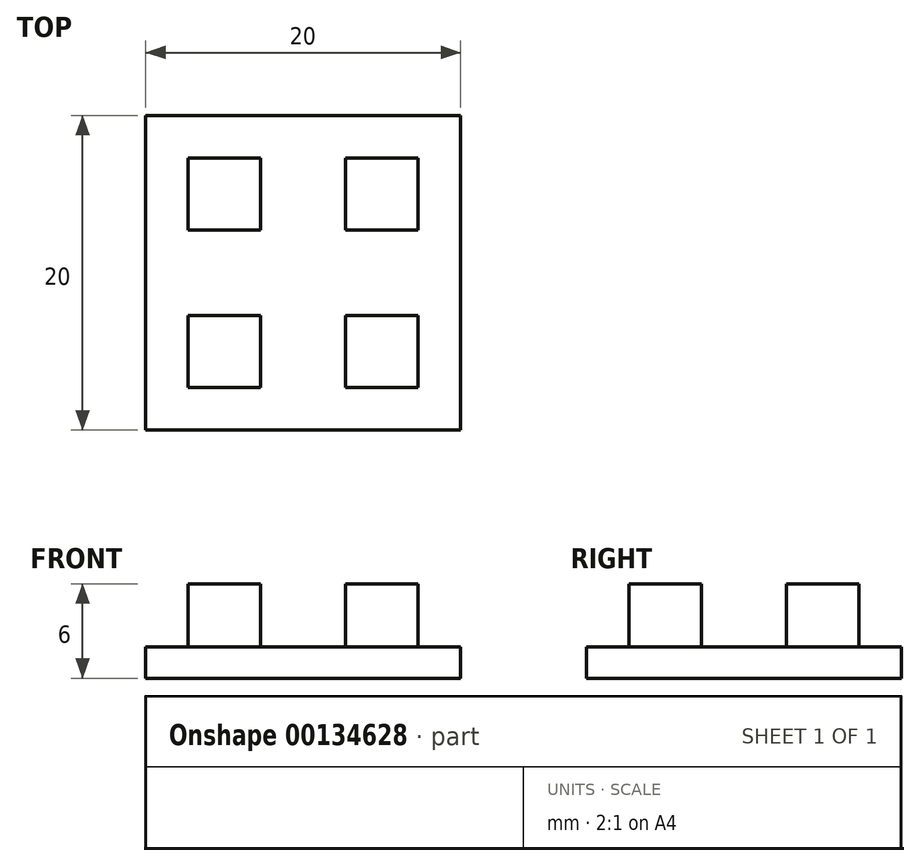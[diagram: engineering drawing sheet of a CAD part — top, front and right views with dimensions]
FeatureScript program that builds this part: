
annotation { "Feature Type Name" : "Feature", "Feature Type Description" : "" }
export const myFeature = defineFeature(function(context is Context, id is Id, definition is map)
    precondition{}
    {
        {
            var Q0;
            Q0=qCreatedBy(makeId("Top.planeOp"),FACE);
            var sketch = newSketch(context, id + "F0", { "sketchPlane" : qUnion([Q0])});
            skLineSegment(sketch, "E0.bottom", {"start": v(10, -10) * mm, "end": v(-10, -10) * mm});
            skLineSegment(sketch, "E0.top", {"start": v(10, 10) * mm, "end": v(-10, 10) * mm});
            skLineSegment(sketch, "E0.left", {"start": v(10, -10) * mm, "end": v(10, 10) * mm});
            skLineSegment(sketch, "E0.right", {"start": v(-10, -10) * mm, "end": v(-10, 10) * mm});
            skPoint(sketch, "E0.middle", {"position": v(0, 0) * mm});
            skLineSegment(sketch, "E1", {"start": v(0, 0) * mm, "end": v(5, 0) * mm});
            skPoint(sketch, "E1.endSnap0", {"position": v(10, 0) * mm});
            skLineSegment(sketch, "E2", {"start": v(5, 0) * mm, "end": v(5, 5) * mm});
            skLineSegment(sketch, "E3.MirrorCS", {"start": v(5, 0) * mm, "end": v(5, -5) * mm});
            skLineSegment(sketch, "E4.MirrorCS", {"start": v(0, 0) * mm, "end": v(-5, 0) * mm});
            skLineSegment(sketch, "E5.MirrorCS", {"start": v(-5, 0) * mm, "end": v(-5, 5) * mm});
            skLineSegment(sketch, "E6.MirrorCS", {"start": v(-5, 0) * mm, "end": v(-5, -5) * mm});
            skLineSegment(sketch, "E7.bottom", {"start": v(7.3, 2.7) * mm, "end": v(2.7, 2.7) * mm});
            skLineSegment(sketch, "E7.top", {"start": v(7.3, 7.3) * mm, "end": v(2.7, 7.3) * mm});
            skLineSegment(sketch, "E7.left", {"start": v(7.3, 2.7) * mm, "end": v(7.3, 7.3) * mm});
            skLineSegment(sketch, "E7.right", {"start": v(2.7, 2.7) * mm, "end": v(2.7, 7.3) * mm});
            skPoint(sketch, "E7.middle", {"position": v(5, 5) * mm});
            skLineSegment(sketch, "E8.MirrorCS", {"start": v(7.3, -2.7) * mm, "end": v(2.7, -2.7) * mm});
            skLineSegment(sketch, "E9.MirrorCS", {"start": v(2.7, -2.7) * mm, "end": v(2.7, -7.3) * mm});
            skLineSegment(sketch, "E10.MirrorCS", {"start": v(7.3, -7.3) * mm, "end": v(2.7, -7.3) * mm});
            skLineSegment(sketch, "E11.MirrorCS", {"start": v(7.3, -2.7) * mm, "end": v(7.3, -7.3) * mm});
            skLineSegment(sketch, "E12.MirrorCS", {"start": v(-2.7, 2.7) * mm, "end": v(-2.7, 7.3) * mm});
            skLineSegment(sketch, "E13.MirrorCS", {"start": v(-7.3, 2.7) * mm, "end": v(-7.3, 7.3) * mm});
            skLineSegment(sketch, "E14.MirrorCS", {"start": v(-7.3, 2.7) * mm, "end": v(-2.7, 2.7) * mm});
            skLineSegment(sketch, "E15.MirrorCS", {"start": v(-7.3, 7.3) * mm, "end": v(-2.7, 7.3) * mm});
            skLineSegment(sketch, "E16.MirrorCS", {"start": v(-2.7, -2.7) * mm, "end": v(-2.7, -7.3) * mm});
            skLineSegment(sketch, "E17.MirrorCS", {"start": v(-7.3, -7.3) * mm, "end": v(-2.7, -7.3) * mm});
            skLineSegment(sketch, "E18.MirrorCS", {"start": v(-7.3, -2.7) * mm, "end": v(-7.3, -7.3) * mm});
            skLineSegment(sketch, "E19.MirrorCS", {"start": v(-7.3, -2.7) * mm, "end": v(-2.7, -2.7) * mm});
            skSolve(sketch);
        }
        {
            var Q0;
            Q0=makeQuery(id+"F0.imprint","IMPRINT",FACE,{"disambiguationData":[TD([[makeQuery(id+"F0.imprint","IMPRINT",EDGE,{"derivedFrom":sQuery(id+"F0.wireOp",EDGE,"E0.bottom")}),-1.0]])]});
            extrude(context, id + "F1", {"entities" : qUnion([Q0]), "depth" : 2 * mm});
        }
        {
            var Q0;
            {var subQ1=sQuery(id+"F0.wireOp",EDGE,"E12.MirrorCS");Q0=makeQuery(id+"F0.imprint","IMPRINT",FACE,{"disambiguationData":[TD([[makeQuery(id+"F0.imprint","IMPRINT",EDGE,{"derivedFrom":subQ1}),1.0]])]});}
            var Q1;
            Q1=makeQuery(id+"F0.imprint","IMPRINT",FACE,{"disambiguationData":[TD([[makeQuery(id+"F0.imprint","IMPRINT",EDGE,{"derivedFrom":sQuery(id+"F0.wireOp",EDGE,"E7.top")}),1.0]])]});
            var Q2;
            {var subQ3=sQuery(id+"F0.wireOp",EDGE,"E16.MirrorCS");Q2=makeQuery(id+"F0.imprint","IMPRINT",FACE,{"disambiguationData":[TD([[makeQuery(id+"F0.imprint","IMPRINT",EDGE,{"derivedFrom":subQ3}),-1.0]])]});}
            var Q3;
            {var subQ0=sQuery(id+"F0.wireOp",EDGE,"E9.MirrorCS");Q3=makeQuery(id+"F0.imprint","IMPRINT",FACE,{"disambiguationData":[TD([[makeQuery(id+"F0.imprint","IMPRINT",EDGE,{"derivedFrom":subQ0}),1.0]])]});}
            extrude(context, id + "F2", {"entities" : qUnion([Q0, Q1, Q2, Q3]), "operationType" : NewBodyOperationType.ADD, "depth" : 6 * mm});
        }
    });
